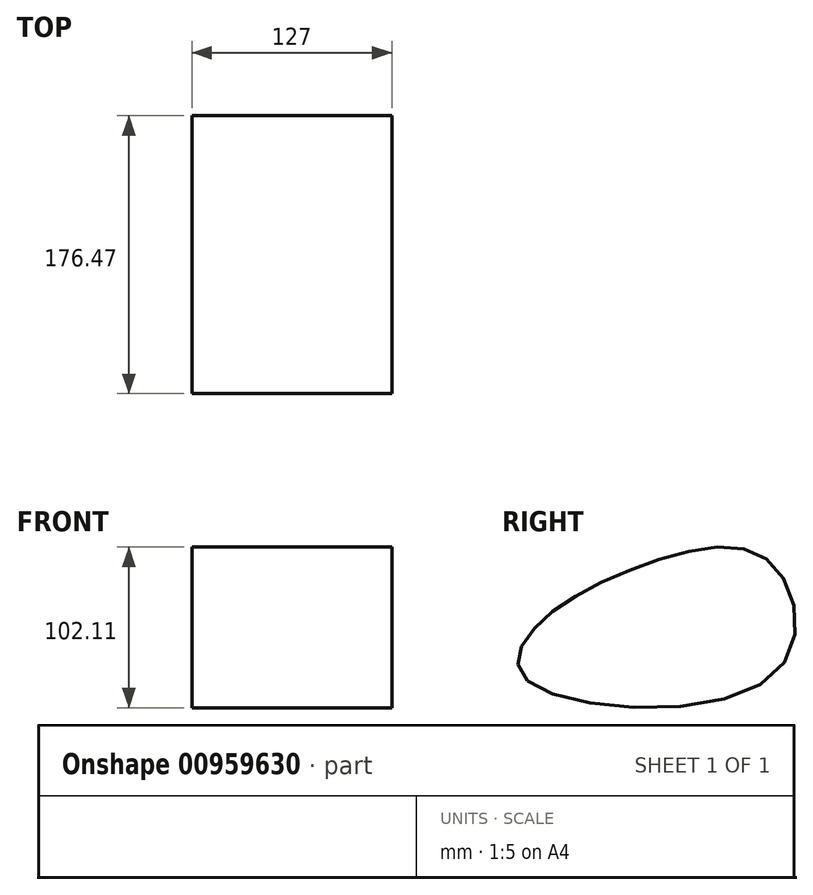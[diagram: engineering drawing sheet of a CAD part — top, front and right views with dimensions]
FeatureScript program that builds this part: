
annotation { "Feature Type Name" : "Feature", "Feature Type Description" : "" }
export const myFeature = defineFeature(function(context is Context, id is Id, definition is map)
    precondition{}
    {
        {
            var Q0;
            Q0=qCreatedBy(makeId("Right.planeOp"),FACE);
            var sketch = newSketch(context, id + "F0", { "sketchPlane" : qUnion([Q0])});
            skFitSpline(sketch, "E0", {"points": [v(-78.2, -75.18) * mm, v(-74.36, -42.5) * mm, v(0, 0) * mm, v(76, 0) * mm, v(77.38, -72.16) * mm, v(-78.2, -75.18) * mm]});
            skFitSpline(sketch, "E1.0", {"points": [v(-73.3, -71) * mm, v(-74.08, -70.36) * mm, v(-74.77, -69.74) * mm, v(-75.57, -68.92) * mm, v(-76.37, -67.93) * mm, v(-77.07, -66.8) * mm, v(-77.54, -65.73) * mm, v(-77.85, -64.65) * mm, v(-78.01, -63.52) * mm, v(-78.02, -62.32) * mm, v(-77.83, -60.56) * mm, v(-77.15, -58.1) * mm, v(-75.58, -54.75) * mm, v(-73.3, -51.18) * mm, v(-70.88, -48.13) * mm, v(-68.7, -45.68) * mm, v(-66.36, -43.25) * mm, v(-63.18, -40.25) * mm, v(-58.95, -36.73) * mm, v(-52.82, -32.14) * mm, v(-44.3, -26.62) * mm, v(-32.92, -20.43) * mm, v(-22.7, -15.65) * mm, v(-14.2, -12.07) * mm, v(-7.7, -9.52) * mm, v(-1.1, -7.09) * mm, v(5.58, -4.78) * mm, v(12.25, -2.66) * mm, v(21.08, -0.13) * mm, v(31.87, 2.32) * mm, v(44.03, 3.7) * mm, v(53.15, 3.25) * mm, v(59.68, 1.84) * mm, v(64.17, 0.24) * mm, v(67.58, -1.58) * mm, v(70.13, -3.36) * mm, v(71.96, -4.85) * mm, v(73.72, -6.55) * mm, v(75.97, -9.07) * mm, v(78.57, -12.67) * mm, v(81.23, -17.59) * mm, v(84.08, -24.77) * mm, v(85.7, -32.6) * mm, v(85.84, -40.52) * mm, v(85.18, -46.37) * mm, v(83.7, -52.02) * mm, v(81.4, -57.37) * mm, v(78.73, -61.52) * mm, v(76.1, -64.62) * mm, v(74.25, -66.46) * mm, v(72.64, -67.87) * mm, v(70.92, -69.25) * mm, v(68.57, -70.91) * mm, v(65.46, -72.8) * mm, v(60.95, -75.16) * mm, v(54.65, -77.8) * mm, v(46.21, -80.46) * mm, v(37.06, -82.6) * mm, v(24.11, -84.76) * mm, v(6.95, -86.17) * mm, v(-13.96, -85.95) * mm, v(-30.6, -84.32) * mm, v(-42.82, -82.25) * mm, v(-51.27, -80.35) * mm, v(-58.83, -78.13) * mm, v(-64.25, -76.06) * mm, v(-67.95, -74.32) * mm, v(-70.4, -72.99) * mm, v(-72.11, -71.88) * mm, v(-73.3, -71) * mm, v(-74.08, -70.36) * mm, v(-74.77, -69.74) * mm, v(-73.3, -71) * mm]});
            skLineSegment(sketch, "E2", {"start": v(-65.54, -42.5) * mm, "end": v(85.57, -42.5) * mm});
            skSolve(sketch);
        }
        {
            var Q0;
            {var subQ0=sQuery(id+"F0.wireOp",EDGE,"E2");Q0=makeQuery(id+"F0.imprint","IMPRINT",FACE,{"disambiguationData":[TD([[makeQuery(id+"F0.imprint","IMPRINT",EDGE,{"derivedFrom":subQ0}),-1.0]])]});}
            var Q1;
            Q1=makeQuery(id+"F0.imprint","IMPRINT",FACE,{"disambiguationData":[TD([[makeQuery(id+"F0.imprint","IMPRINT",EDGE,{"derivedFrom":sQuery(id+"F0.wireOp",EDGE,"E0")}),-1.0]])]});
            var Q2;
            Q2 = qBodyType(qCreatedBy(id + "F0" ,EDGE), BodyType.WIRE);
            var Q3;
            Q3=sQuery(id+"F0.wireOp",EDGE,"E1.0");
            extrude(context, id + "F1", {"entities" : qUnion([Q0, Q1]), "surfaceEntities" : qUnion([Q2, Q3]), "endBound" : BoundingType.SYMMETRIC, "depth" : 127 * mm, "offsetDistance" : 25.4 * mm});
        }
    });
